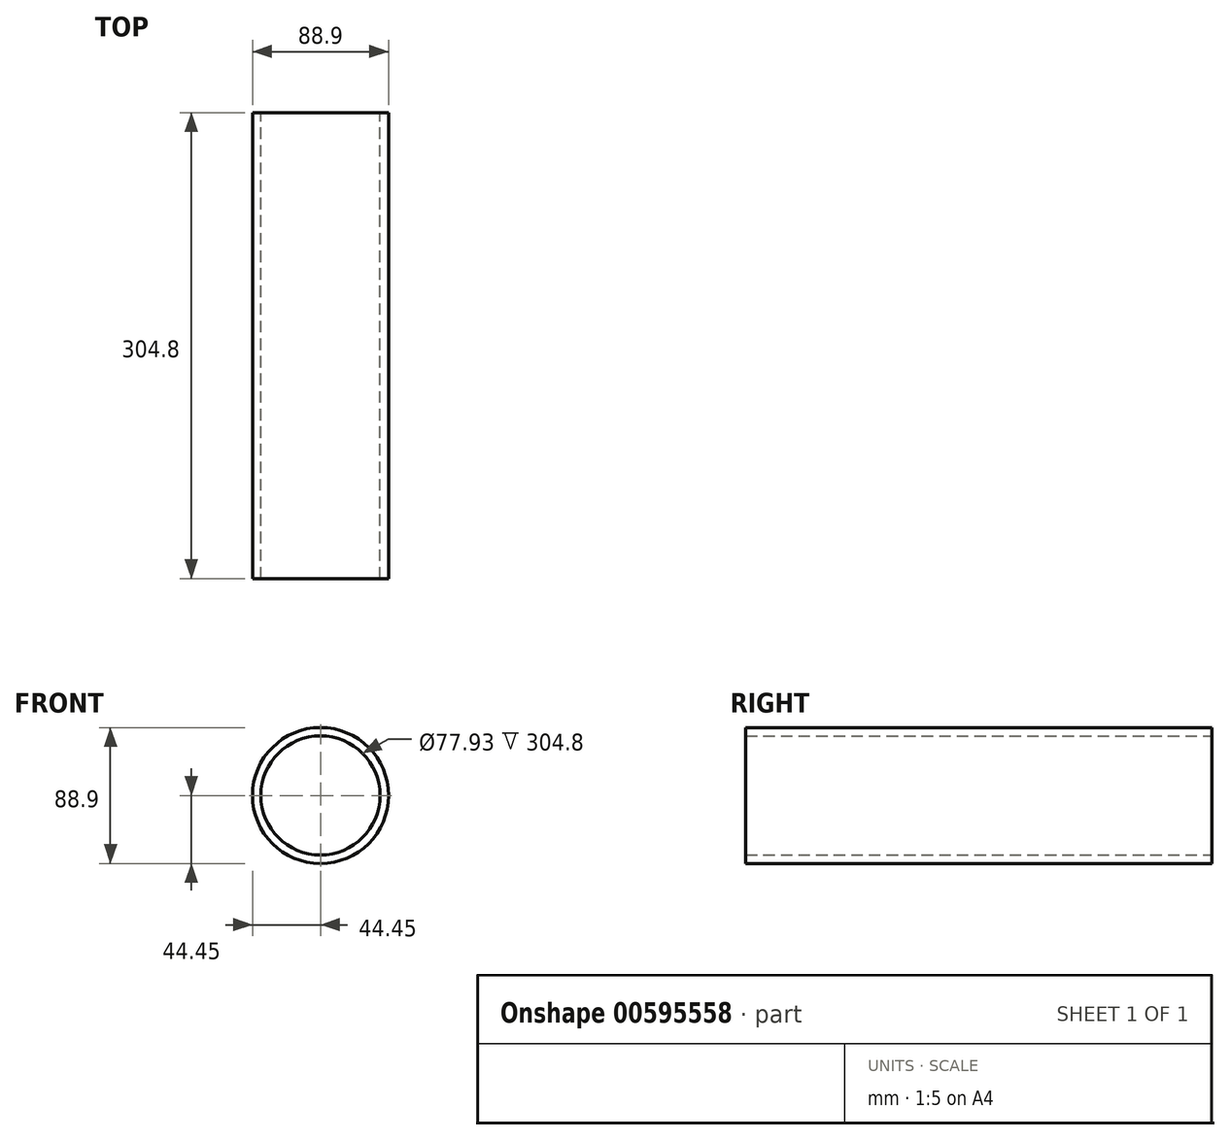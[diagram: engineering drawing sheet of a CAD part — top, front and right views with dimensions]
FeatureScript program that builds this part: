
annotation { "Feature Type Name" : "Feature", "Feature Type Description" : "" }
export const myFeature = defineFeature(function(context is Context, id is Id, definition is map)
    precondition{}
    {
        {
            var Q0;
            Q0=qCreatedBy(makeId("Front.planeOp"),FACE);
            var sketch = newSketch(context, id + "F0", { "sketchPlane" : qUnion([Q0])});
            skCircle(sketch, "E0", {"center": v(0, 0) * mm, "radius": 44.45 * mm});
            skCircle(sketch, "E1", {"center": v(0, 0) * mm, "radius": 38.96 * mm});
            skSolve(sketch);
        }
        {
            var Q0;
            Q0 = qSketchRegion(id + "F0", true);
            extrude(context, id + "F1", {"entities" : qUnion([Q0]), "depth" : 304.8 * mm, "offsetDistance" : 25.4 * mm});
        }
    });
